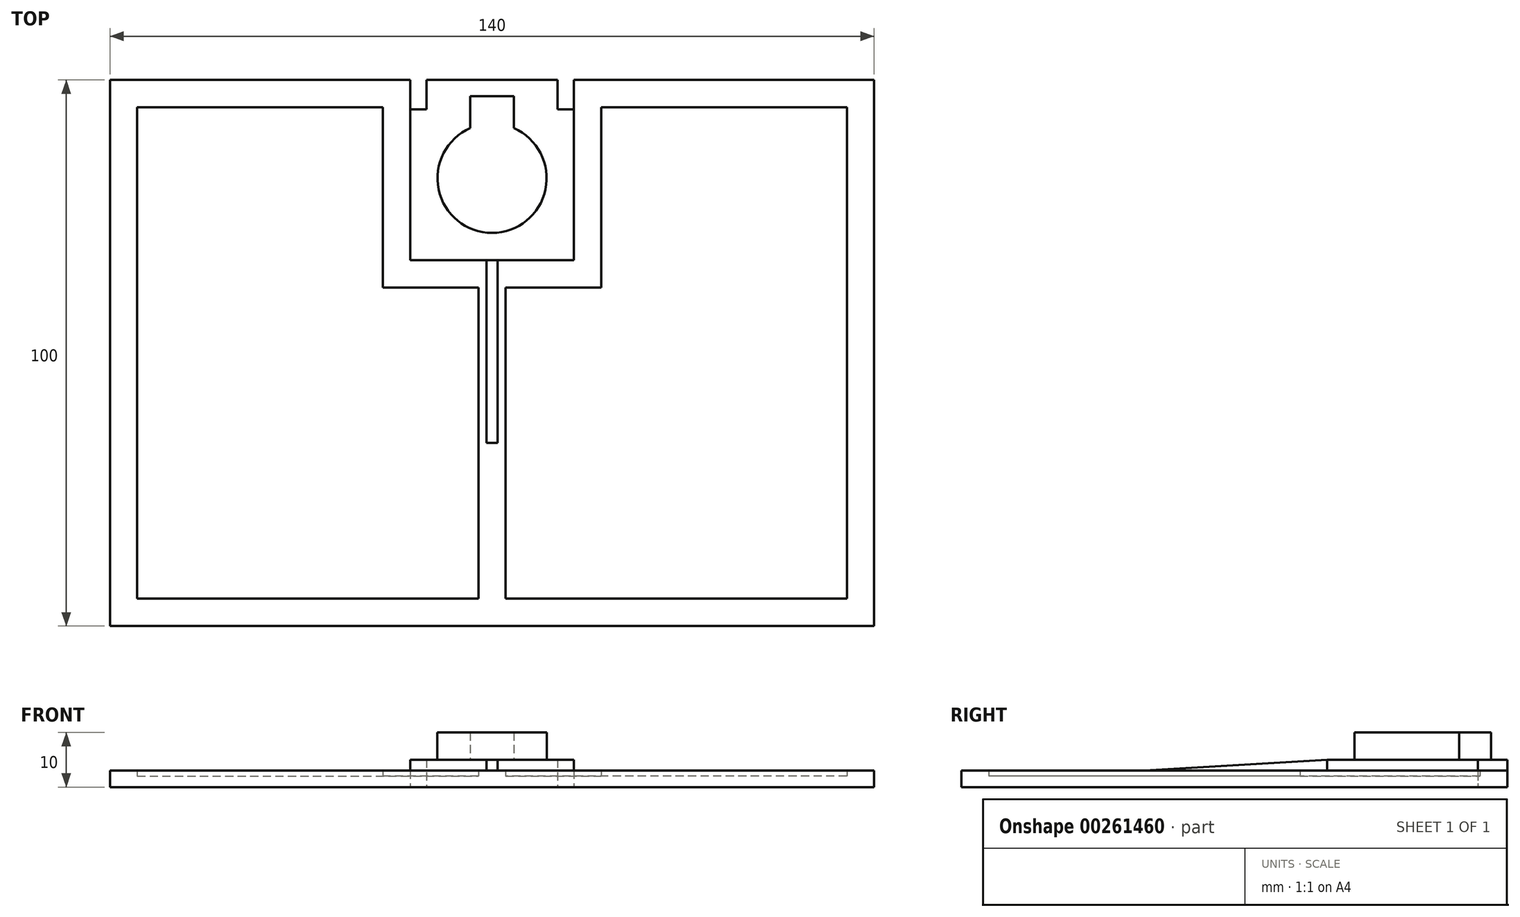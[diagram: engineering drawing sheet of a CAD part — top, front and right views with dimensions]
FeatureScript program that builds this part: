
annotation { "Feature Type Name" : "Feature", "Feature Type Description" : "" }
export const myFeature = defineFeature(function(context is Context, id is Id, definition is map)
    precondition{}
    {
        {
            var Q0;
            Q0=qCreatedBy(makeId("Top.planeOp"),FACE);
            var sketch = newSketch(context, id + "F0", { "sketchPlane" : qUnion([Q0])});
            skLineSegment(sketch, "E0.top", {"start": v(-15, -15) * mm, "end": v(15, -15) * mm});
            skLineSegment(sketch, "E0.left", {"start": v(-15, 22.6) * mm, "end": v(-15, -15) * mm});
            skLineSegment(sketch, "E0.right", {"start": v(15, 22.6) * mm, "end": v(15, -15) * mm});
            skCircle(sketch, "E1", {"center": v(0, 0) * mm, "radius": 10 * mm});
            skLineSegment(sketch, "E2.bottom", {"start": v(-4, 15) * mm, "end": v(4, 15) * mm});
            skLineSegment(sketch, "E2.top", {"start": v(-4, 0) * mm, "end": v(4, 0) * mm});
            skLineSegment(sketch, "E2.left", {"start": v(-4, 15) * mm, "end": v(-4, 0) * mm});
            skLineSegment(sketch, "E2.right", {"start": v(4, 15) * mm, "end": v(4, 0) * mm});
            skLineSegment(sketch, "E3.bottom", {"start": v(-15, 22.6) * mm, "end": v(-12, 22.6) * mm});
            skLineSegment(sketch, "E3.top", {"start": v(-15, 12.6) * mm, "end": v(-12, 12.6) * mm});
            skLineSegment(sketch, "E3.left", {"start": v(-15, 22.6) * mm, "end": v(-15, 12.6) * mm});
            skLineSegment(sketch, "E3.right", {"start": v(-12, 22.6) * mm, "end": v(-12, 12.6) * mm});
            skLineSegment(sketch, "E4.MirrorCS", {"start": v(15, 12.6) * mm, "end": v(12, 12.6) * mm});
            skLineSegment(sketch, "E5.MirrorCS", {"start": v(12, 22.6) * mm, "end": v(12, 12.6) * mm});
            skLineSegment(sketch, "E6.MirrorCS", {"start": v(15, 22.6) * mm, "end": v(15, 12.6) * mm});
            skLineSegment(sketch, "E7.MirrorCS", {"start": v(15, 22.6) * mm, "end": v(12, 22.6) * mm});
            skLineSegment(sketch, "E8.bottom", {"start": v(-70, 18) * mm, "end": v(70, 18) * mm});
            skLineSegment(sketch, "E8.top", {"start": v(-70, -82) * mm, "end": v(70, -82) * mm});
            skLineSegment(sketch, "E8.left", {"start": v(-70, 18) * mm, "end": v(-70, -82) * mm});
            skLineSegment(sketch, "E8.right", {"start": v(70, 18) * mm, "end": v(70, -82) * mm});
            skLineSegment(sketch, "E9.top", {"start": v(-65, -77) * mm, "end": v(-2.5, -77) * mm});
            skLineSegment(sketch, "E9.left", {"start": v(-65, 13) * mm, "end": v(-65, -77) * mm});
            skLineSegment(sketch, "E10", {"start": v(-2.5, -20) * mm, "end": v(-20, -20) * mm});
            skLineSegment(sketch, "E11", {"start": v(-20, -20) * mm, "end": v(-20, 13) * mm});
            skLineSegment(sketch, "E12", {"start": v(-65, 13) * mm, "end": v(-20, 13) * mm});
            skLineSegment(sketch, "E13", {"start": v(-2.5, -20) * mm, "end": v(-2.5, -77) * mm});
            skLineSegment(sketch, "E14.MirrorCS", {"start": v(20, -20) * mm, "end": v(20, 13) * mm});
            skLineSegment(sketch, "E15.MirrorCS", {"start": v(2.5, -20) * mm, "end": v(20, -20) * mm});
            skLineSegment(sketch, "E16.MirrorCS", {"start": v(2.5, -20) * mm, "end": v(2.5, -77) * mm});
            skLineSegment(sketch, "E17.MirrorCS", {"start": v(65, -77) * mm, "end": v(2.5, -77) * mm});
            skLineSegment(sketch, "E18.MirrorCS", {"start": v(65, 13) * mm, "end": v(20, 13) * mm});
            skLineSegment(sketch, "E19.MirrorCS", {"start": v(65, 13) * mm, "end": v(65, -77) * mm});
            skSolve(sketch);
        }
        {
            var Q0;
            Q0=makeQuery(id+"F0.imprint","IMPRINT",FACE,{"disambiguationData":[TD([[makeQuery(id+"F0.imprint","IMPRINT",EDGE,{"derivedFrom":sQuery(id+"F0.wireOp",EDGE,"E0.top")}),-1.0]])]});
            var Q1;
            Q1=makeQuery(id+"F0.imprint","IMPRINT",FACE,{"disambiguationData":[TD([[makeQuery(id+"F0.imprint","IMPRINT",EDGE,{"derivedFrom":sQuery(id+"F0.wireOp",EDGE,"E0.top")}),1.0]])]});
            extrude(context, id + "F1", {"entities" : qUnion([Q0, Q1]), "depth" : 3 * mm});
        }
        {
            var Q0;
            Q0=makeQuery(id+"F0.imprint","IMPRINT",FACE,{"disambiguationData":[TD([[makeQuery(id+"F0.imprint","IMPRINT",EDGE,{"derivedFrom":sQuery(id+"F0.wireOp",EDGE,"E0.top")}),1.0]])]});
            extrude(context, id + "F2", {"entities" : qUnion([Q0]), "operationType" : NewBodyOperationType.ADD, "depth" : 5 * mm});
        }
        {
            var Q0;
            {var subQ5=sQuery(id+"F0.wireOp",EDGE,"E2.bottom");Q0=makeQuery(id+"F0.imprint","IMPRINT",FACE,{"disambiguationData":[TD([[makeQuery(id+"F0.imprint","IMPRINT",EDGE,{"derivedFrom":subQ5}),-1.0]])]});}
            var Q1;
            {var subQ5=sQuery(id+"F0.wireOp",EDGE,"E2.top");Q1=makeQuery(id+"F0.imprint","IMPRINT",FACE,{"disambiguationData":[TD([[makeQuery(id+"F0.imprint","IMPRINT",EDGE,{"derivedFrom":subQ5}),1.0]])]});}
            var Q2;
            {var subQ5=sQuery(id+"F0.wireOp",EDGE,"E2.top");Q2=makeQuery(id+"F0.imprint","IMPRINT",FACE,{"disambiguationData":[TD([[makeQuery(id+"F0.imprint","IMPRINT",EDGE,{"derivedFrom":subQ5}),-1.0]])]});}
            extrude(context, id + "F3", {"entities" : qUnion([Q0, Q1, Q2]), "operationType" : NewBodyOperationType.ADD, "depth" : 10 * mm});
        }
        {
            var Q0;
            Q0=qCreatedBy(makeId("Right.planeOp"),FACE);
            var sketch = newSketch(context, id + "F4", { "sketchPlane" : qUnion([Q0])});
            skPoint(sketch, "E20.0", {"position": v(-15, 5) * mm});
            skPoint(sketch, "E21.0", {"position": v(-48.5, 3) * mm});
            skPoint(sketch, "E22.0", {"position": v(-15, 3) * mm});
            skLineSegment(sketch, "E23", {"start": v(-15, 5) * mm, "end": v(-48.5, 3) * mm});
            skLineSegment(sketch, "E24", {"start": v(-15, 5) * mm, "end": v(-15, 3) * mm});
            skLineSegment(sketch, "E25", {"start": v(-48.5, 3) * mm, "end": v(-15, 3) * mm});
            skSolve(sketch);
        }
        {
            var Q0;
            Q0=makeQuery(id+"F4.imprint","IMPRINT",FACE,{"disambiguationData":[TD([[makeQuery(id+"F4.imprint","IMPRINT",EDGE,{"derivedFrom":sQuery(id+"F4.wireOp",EDGE,"E23")}),1.0]])]});
            extrude(context, id + "F5", {"entities" : qUnion([Q0]), "operationType" : NewBodyOperationType.ADD, "endBound" : BoundingType.SYMMETRIC, "oppositeDirection" : true, "depth" : 2 * mm});
        }
        {
            var Q0;
            Q0=makeQuery(id+"F0.imprint","IMPRINT",FACE,{"disambiguationData":[TD([[makeQuery(id+"F0.imprint","IMPRINT",EDGE,{"derivedFrom":sQuery(id+"F0.wireOp",EDGE,"E9.top")}),1.0]])]});
            var Q1;
            Q1=makeQuery(id+"F0.imprint","IMPRINT",FACE,{"disambiguationData":[TD([[makeQuery(id+"F0.imprint","IMPRINT",EDGE,{"derivedFrom":sQuery(id+"F0.wireOp",EDGE,"E14.MirrorCS")}),-1.0]])]});
            extrude(context, id + "F6", {"entities" : qUnion([Q0, Q1]), "operationType" : NewBodyOperationType.ADD, "depth" : 2 * mm});
        }
    });
